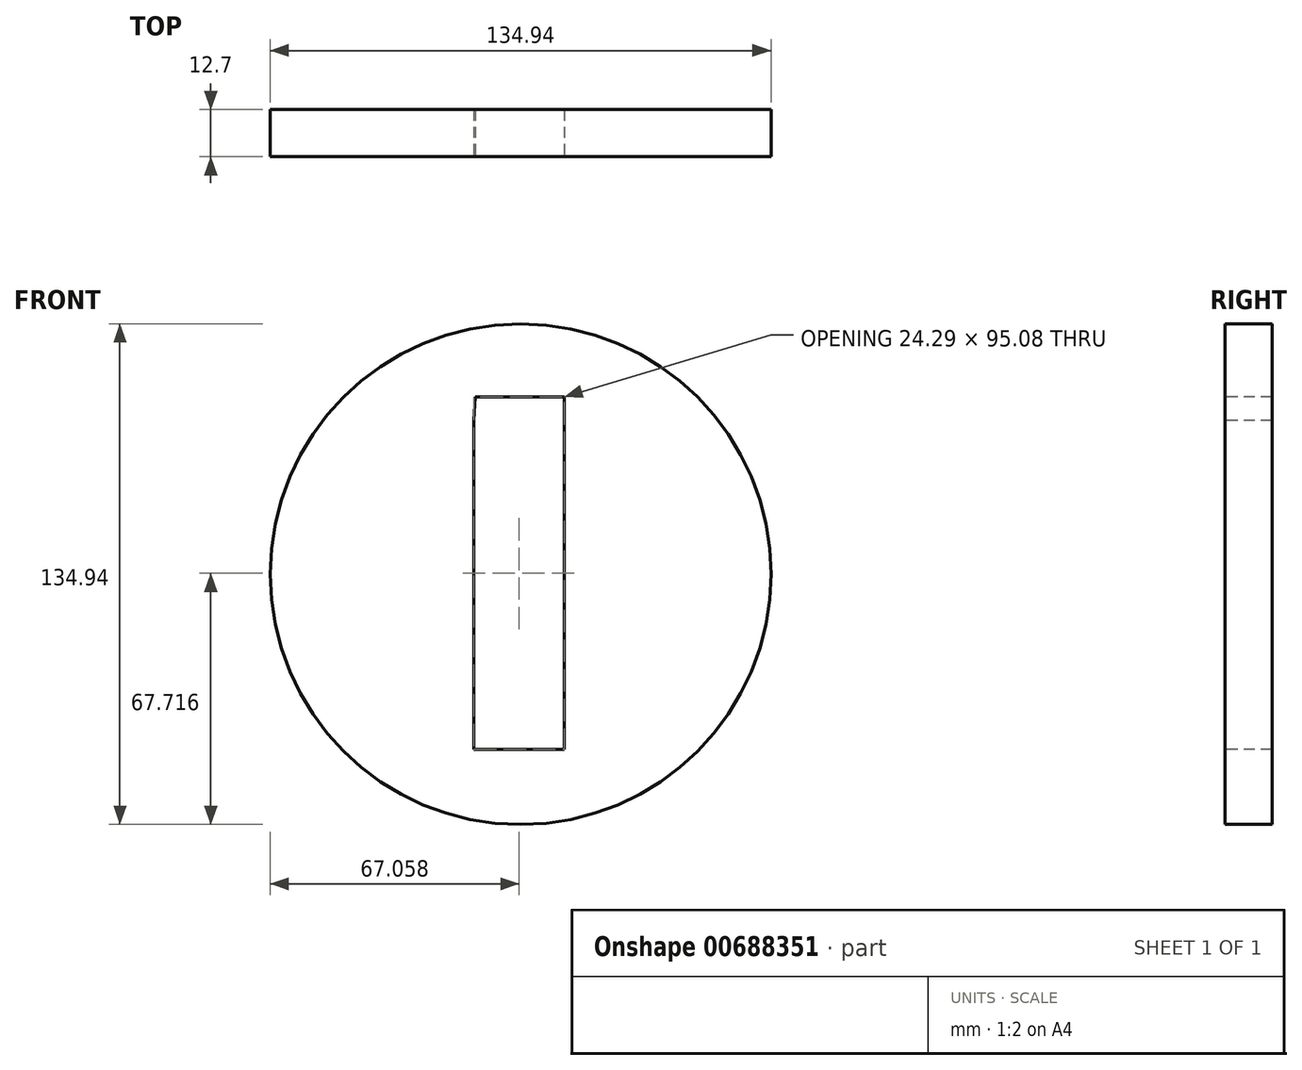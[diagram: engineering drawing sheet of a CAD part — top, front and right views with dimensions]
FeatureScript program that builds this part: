
annotation { "Feature Type Name" : "Feature", "Feature Type Description" : "" }
export const myFeature = defineFeature(function(context is Context, id is Id, definition is map)
    precondition{}
    {
        {
            var Q0;
            Q0=qCreatedBy(makeId("Front.planeOp"),FACE);
            var sketch = newSketch(context, id + "F0", { "sketchPlane" : qUnion([Q0])});
            skCircle(sketch, "E0", {"center": v(0, 0) * mm, "radius": 67.47 * mm});
            skSolve(sketch);
        }
        {
            var Q0;
            Q0=makeQuery(id+"F0.imprint","IMPRINT",FACE,{"disambiguationData":[TD([[makeQuery(id+"F0.imprint","IMPRINT",EDGE,{"derivedFrom":sQuery(id+"F0.wireOp",EDGE,"E0")}),1.0]])]});
            extrude(context, id + "F1", {"entities" : qUnion([Q0]), "depth" : 12.7 * mm, "offsetDistance" : 25.4 * mm});
        }
        {
            var Q0;
            Q0=makeQuery(id+"F1.opExtrude","CAP_FACE",FACE,{"disambiguationData":[OSD([sQuery(id+"F0.wireOp",EDGE,"E0")])],"isStart":false});
            var sketch = newSketch(context, id + "F2", { "sketchPlane" : qUnion([Q0])});
            skLineSegment(sketch, "E1", {"start": v(-12.56, 41.4) * mm, "end": v(-12.56, -47.3) * mm});
            skLineSegment(sketch, "E2", {"start": v(-12.56, -47.3) * mm, "end": v(11.74, -47.3) * mm});
            skLineSegment(sketch, "E3", {"start": v(11.74, -47.3) * mm, "end": v(11.74, 47.79) * mm});
            skLineSegment(sketch, "E4", {"start": v(11.74, 47.79) * mm, "end": v(-12.26, 47.79) * mm});
            skLineSegment(sketch, "E5", {"start": v(-12.26, 47.79) * mm, "end": v(-12.56, 41.4) * mm});
            skSolve(sketch);
        }
        {
            var Q0;
            Q0=makeQuery(id+"F2.imprint","IMPRINT",FACE,{"disambiguationData":[TD([[makeQuery(id+"F2.imprint","IMPRINT",EDGE,{"derivedFrom":sQuery(id+"F2.wireOp",EDGE,"E1")}),1.0]])]});
            extrude(context, id + "F3", {"entities" : qUnion([Q0]), "operationType" : NewBodyOperationType.REMOVE, "oppositeDirection" : true, "depth" : 12.7 * mm, "offsetDistance" : 25.4 * mm});
        }
    });
